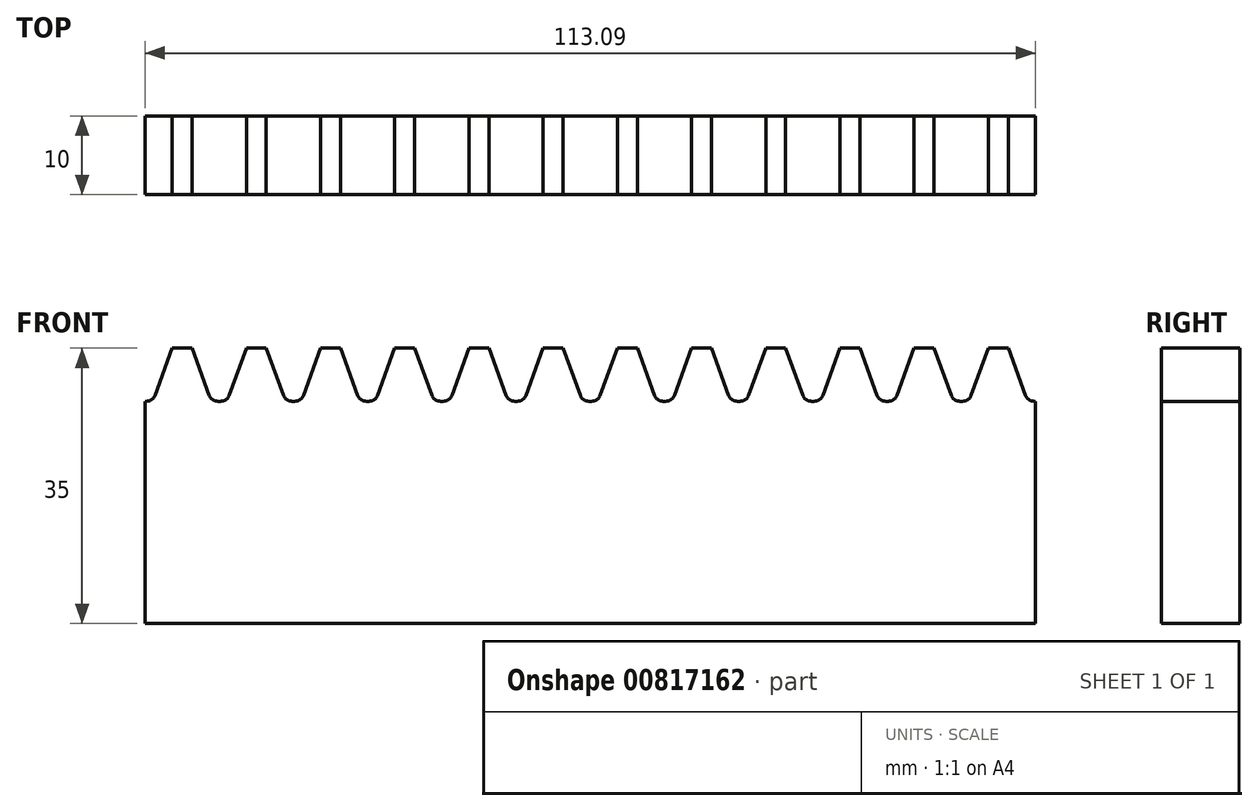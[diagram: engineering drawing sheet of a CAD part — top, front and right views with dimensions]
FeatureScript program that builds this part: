
annotation { "Feature Type Name" : "Feature", "Feature Type Description" : "" }
export const myFeature = defineFeature(function(context is Context, id is Id, definition is map)
    precondition{}
    {
        {
            assignVariable(context, id + "F0", {"name" : "Width", "anyValue" : 10 * mm});
        }
        {
            var Q0;
            Q0=qCreatedBy(makeId("Front.planeOp"),FACE);
            var sketch = newSketch(context, id + "F1", { "sketchPlane" : qUnion([Q0])});
            skLineSegment(sketch, "E0", {"start": v(1.26, 35) * mm, "end": v(-1.26, 35) * mm});
            skLineSegment(sketch, "E1", {"start": v(-4.71, 0) * mm, "end": v(4.71, 0) * mm});
            skLineSegment(sketch, "E2", {"start": v(-4.71, 28.25) * mm, "end": v(-4.52, 28.25) * mm});
            skLineSegment(sketch, "E3", {"start": v(-3.45, 29) * mm, "end": v(-1.26, 35) * mm});
            skLineSegment(sketch, "E4", {"start": v(-4.71, 28.25) * mm, "end": v(-4.71, 0) * mm});
            skLineSegment(sketch, "E5", {"start": v(-2.36, 32) * mm, "end": v(2.36, 32) * mm, "construction": true});
            skLineSegment(sketch, "E6", {"start": v(0, 35) * mm, "end": v(0, 0) * mm, "construction": true});
            skPoint(sketch, "E7.visualSharp", {"position": v(-3.72, 28.25) * mm});
            skArc(sketch, "E7.filletArc", {"start": v(-4.52, 28.25) * mm, "mid": v(-3.87, 28.46) * mm, "end": v(-3.45, 29) * mm});
            skLineSegment(sketch, "E8.MirrorCS", {"start": v(3.45, 29) * mm, "end": v(1.26, 35) * mm});
            skArc(sketch, "E9.MirrorCS", {"start": v(4.52, 28.25) * mm, "mid": v(3.87, 28.46) * mm, "end": v(3.45, 29) * mm});
            skLineSegment(sketch, "E10.MirrorCS", {"start": v(4.71, 28.25) * mm, "end": v(4.52, 28.25) * mm});
            skLineSegment(sketch, "E11.MirrorCS", {"start": v(4.71, 28.25) * mm, "end": v(4.71, 0) * mm});
            skLineSegment(sketch, "E12.1.0.0", {"start": v(9.42, 35) * mm, "end": v(9.42, 0) * mm, "construction": true});
            skPoint(sketch, "E12.1.0.2", {"position": v(5.7, 28.25) * mm});
            skLineSegment(sketch, "E12.1.0.3", {"start": v(14.14, 28.25) * mm, "end": v(14.14, 0) * mm});
            skLineSegment(sketch, "E12.1.0.4", {"start": v(12.87, 29) * mm, "end": v(10.69, 35) * mm});
            skLineSegment(sketch, "E12.1.0.5", {"start": v(4.71, 0) * mm, "end": v(14.14, 0) * mm});
            skLineSegment(sketch, "E12.1.0.6", {"start": v(7.07, 32) * mm, "end": v(11.78, 32) * mm, "construction": true});
            skLineSegment(sketch, "E12.1.0.7", {"start": v(5.98, 29) * mm, "end": v(8.16, 35) * mm});
            skLineSegment(sketch, "E12.1.0.8", {"start": v(10.69, 35) * mm, "end": v(8.16, 35) * mm});
            skArc(sketch, "E12.1.0.9", {"start": v(13.94, 28.25) * mm, "mid": v(13.3, 28.46) * mm, "end": v(12.87, 29) * mm});
            skLineSegment(sketch, "E12.1.0.10", {"start": v(14.14, 28.25) * mm, "end": v(13.94, 28.25) * mm});
            skArc(sketch, "E12.1.0.11", {"start": v(4.9, 28.25) * mm, "mid": v(5.56, 28.46) * mm, "end": v(5.98, 29) * mm});
            skLineSegment(sketch, "E12.1.0.12", {"start": v(4.71, 28.25) * mm, "end": v(4.9, 28.25) * mm});
            skLineSegment(sketch, "E12.2.0.0", {"start": v(18.85, 35) * mm, "end": v(18.85, 0) * mm, "construction": true});
            skLineSegment(sketch, "E12.2.0.1", {"start": v(14.14, 28.25) * mm, "end": v(14.14, 0) * mm});
            skPoint(sketch, "E12.2.0.2", {"position": v(15.13, 28.25) * mm});
            skLineSegment(sketch, "E12.2.0.3", {"start": v(23.56, 28.25) * mm, "end": v(23.56, 0) * mm});
            skLineSegment(sketch, "E12.2.0.4", {"start": v(22.3, 29) * mm, "end": v(20.11, 35) * mm});
            skLineSegment(sketch, "E12.2.0.5", {"start": v(14.14, 0) * mm, "end": v(23.56, 0) * mm});
            skLineSegment(sketch, "E12.2.0.6", {"start": v(16.5, 32) * mm, "end": v(21.2, 32) * mm, "construction": true});
            skLineSegment(sketch, "E12.2.0.7", {"start": v(15.4, 29) * mm, "end": v(17.59, 35) * mm});
            skLineSegment(sketch, "E12.2.0.8", {"start": v(20.11, 35) * mm, "end": v(17.59, 35) * mm});
            skArc(sketch, "E12.2.0.9", {"start": v(23.37, 28.25) * mm, "mid": v(22.71, 28.46) * mm, "end": v(22.3, 29) * mm});
            skLineSegment(sketch, "E12.2.0.10", {"start": v(23.56, 28.25) * mm, "end": v(23.37, 28.25) * mm});
            skArc(sketch, "E12.2.0.11", {"start": v(14.33, 28.25) * mm, "mid": v(14.98, 28.46) * mm, "end": v(15.4, 29) * mm});
            skLineSegment(sketch, "E12.2.0.12", {"start": v(14.14, 28.25) * mm, "end": v(14.33, 28.25) * mm});
            skLineSegment(sketch, "E12.3.0.0", {"start": v(28.27, 35) * mm, "end": v(28.27, 0) * mm, "construction": true});
            skLineSegment(sketch, "E12.3.0.1", {"start": v(23.56, 28.25) * mm, "end": v(23.56, 0) * mm});
            skPoint(sketch, "E12.3.0.2", {"position": v(24.55, 28.25) * mm});
            skLineSegment(sketch, "E12.3.0.3", {"start": v(32.99, 28.25) * mm, "end": v(32.99, 0) * mm});
            skLineSegment(sketch, "E12.3.0.4", {"start": v(31.72, 29) * mm, "end": v(29.54, 35) * mm});
            skLineSegment(sketch, "E12.3.0.5", {"start": v(23.56, 0) * mm, "end": v(32.99, 0) * mm});
            skLineSegment(sketch, "E12.3.0.6", {"start": v(25.92, 32) * mm, "end": v(30.63, 32) * mm, "construction": true});
            skLineSegment(sketch, "E12.3.0.7", {"start": v(24.83, 29) * mm, "end": v(27.01, 35) * mm});
            skLineSegment(sketch, "E12.3.0.8", {"start": v(29.54, 35) * mm, "end": v(27.01, 35) * mm});
            skArc(sketch, "E12.3.0.9", {"start": v(32.8, 28.25) * mm, "mid": v(32.14, 28.46) * mm, "end": v(31.72, 29) * mm});
            skLineSegment(sketch, "E12.3.0.10", {"start": v(32.99, 28.25) * mm, "end": v(32.8, 28.25) * mm});
            skArc(sketch, "E12.3.0.11", {"start": v(23.76, 28.25) * mm, "mid": v(24.4, 28.46) * mm, "end": v(24.83, 29) * mm});
            skLineSegment(sketch, "E12.3.0.12", {"start": v(23.56, 28.25) * mm, "end": v(23.76, 28.25) * mm});
            skLineSegment(sketch, "E12.4.0.0", {"start": v(37.7, 35) * mm, "end": v(37.7, 0) * mm, "construction": true});
            skLineSegment(sketch, "E12.4.0.1", {"start": v(32.99, 28.25) * mm, "end": v(32.99, 0) * mm});
            skPoint(sketch, "E12.4.0.2", {"position": v(33.98, 28.25) * mm});
            skLineSegment(sketch, "E12.4.0.3", {"start": v(42.41, 28.25) * mm, "end": v(42.41, 0) * mm});
            skLineSegment(sketch, "E12.4.0.4", {"start": v(41.15, 29) * mm, "end": v(38.96, 35) * mm});
            skLineSegment(sketch, "E12.4.0.5", {"start": v(32.99, 0) * mm, "end": v(42.41, 0) * mm});
            skLineSegment(sketch, "E12.4.0.6", {"start": v(35.34, 32) * mm, "end": v(40.06, 32) * mm, "construction": true});
            skLineSegment(sketch, "E12.4.0.7", {"start": v(34.25, 29) * mm, "end": v(36.43, 35) * mm});
            skLineSegment(sketch, "E12.4.0.8", {"start": v(38.96, 35) * mm, "end": v(36.43, 35) * mm});
            skArc(sketch, "E12.4.0.9", {"start": v(42.22, 28.25) * mm, "mid": v(41.56, 28.46) * mm, "end": v(41.15, 29) * mm});
            skLineSegment(sketch, "E12.4.0.10", {"start": v(42.41, 28.25) * mm, "end": v(42.22, 28.25) * mm});
            skArc(sketch, "E12.4.0.11", {"start": v(33.18, 28.25) * mm, "mid": v(33.83, 28.46) * mm, "end": v(34.25, 29) * mm});
            skLineSegment(sketch, "E12.4.0.12", {"start": v(32.99, 28.25) * mm, "end": v(33.18, 28.25) * mm});
            skLineSegment(sketch, "E12.5.0.0", {"start": v(47.12, 35) * mm, "end": v(47.12, 0) * mm, "construction": true});
            skLineSegment(sketch, "E12.5.0.1", {"start": v(42.41, 28.25) * mm, "end": v(42.41, 0) * mm});
            skPoint(sketch, "E12.5.0.2", {"position": v(43.4, 28.25) * mm});
            skLineSegment(sketch, "E12.5.0.3", {"start": v(51.84, 28.25) * mm, "end": v(51.84, 0) * mm});
            skLineSegment(sketch, "E12.5.0.4", {"start": v(50.57, 29) * mm, "end": v(48.39, 35) * mm});
            skLineSegment(sketch, "E12.5.0.5", {"start": v(42.41, 0) * mm, "end": v(51.84, 0) * mm});
            skLineSegment(sketch, "E12.5.0.6", {"start": v(44.77, 32) * mm, "end": v(49.48, 32) * mm, "construction": true});
            skLineSegment(sketch, "E12.5.0.7", {"start": v(43.68, 29) * mm, "end": v(45.86, 35) * mm});
            skLineSegment(sketch, "E12.5.0.8", {"start": v(48.39, 35) * mm, "end": v(45.86, 35) * mm});
            skArc(sketch, "E12.5.0.9", {"start": v(51.64, 28.25) * mm, "mid": v(50.99, 28.46) * mm, "end": v(50.57, 29) * mm});
            skLineSegment(sketch, "E12.5.0.10", {"start": v(51.84, 28.25) * mm, "end": v(51.64, 28.25) * mm});
            skArc(sketch, "E12.5.0.11", {"start": v(42.6, 28.25) * mm, "mid": v(43.26, 28.46) * mm, "end": v(43.68, 29) * mm});
            skLineSegment(sketch, "E12.5.0.12", {"start": v(42.41, 28.25) * mm, "end": v(42.6, 28.25) * mm});
            skLineSegment(sketch, "E12.6.0.0", {"start": v(56.55, 35) * mm, "end": v(56.55, 0) * mm, "construction": true});
            skLineSegment(sketch, "E12.6.0.1", {"start": v(51.84, 28.25) * mm, "end": v(51.84, 0) * mm});
            skPoint(sketch, "E12.6.0.2", {"position": v(52.83, 28.25) * mm});
            skLineSegment(sketch, "E12.6.0.3", {"start": v(61.26, 28.25) * mm, "end": v(61.26, 0) * mm});
            skLineSegment(sketch, "E12.6.0.4", {"start": v(60, 29) * mm, "end": v(57.81, 35) * mm});
            skLineSegment(sketch, "E12.6.0.5", {"start": v(51.84, 0) * mm, "end": v(61.26, 0) * mm});
            skLineSegment(sketch, "E12.6.0.6", {"start": v(54.2, 32) * mm, "end": v(58.9, 32) * mm, "construction": true});
            skLineSegment(sketch, "E12.6.0.7", {"start": v(53.1, 29) * mm, "end": v(55.28, 35) * mm});
            skLineSegment(sketch, "E12.6.0.8", {"start": v(57.81, 35) * mm, "end": v(55.28, 35) * mm});
            skArc(sketch, "E12.6.0.9", {"start": v(61.07, 28.25) * mm, "mid": v(60.41, 28.46) * mm, "end": v(60, 29) * mm});
            skLineSegment(sketch, "E12.6.0.10", {"start": v(61.26, 28.25) * mm, "end": v(61.07, 28.25) * mm});
            skArc(sketch, "E12.6.0.11", {"start": v(52.03, 28.25) * mm, "mid": v(52.68, 28.46) * mm, "end": v(53.1, 29) * mm});
            skLineSegment(sketch, "E12.6.0.12", {"start": v(51.84, 28.25) * mm, "end": v(52.03, 28.25) * mm});
            skLineSegment(sketch, "E12.7.0.0", {"start": v(65.97, 35) * mm, "end": v(65.97, 0) * mm, "construction": true});
            skLineSegment(sketch, "E12.7.0.1", {"start": v(61.26, 28.25) * mm, "end": v(61.26, 0) * mm});
            skPoint(sketch, "E12.7.0.2", {"position": v(62.25, 28.25) * mm});
            skLineSegment(sketch, "E12.7.0.3", {"start": v(70.69, 28.25) * mm, "end": v(70.69, 0) * mm});
            skLineSegment(sketch, "E12.7.0.4", {"start": v(69.42, 29) * mm, "end": v(67.24, 35) * mm});
            skLineSegment(sketch, "E12.7.0.5", {"start": v(61.26, 0) * mm, "end": v(70.69, 0) * mm});
            skLineSegment(sketch, "E12.7.0.6", {"start": v(63.62, 32) * mm, "end": v(68.33, 32) * mm, "construction": true});
            skLineSegment(sketch, "E12.7.0.7", {"start": v(62.53, 29) * mm, "end": v(64.7, 35) * mm});
            skLineSegment(sketch, "E12.7.0.8", {"start": v(67.24, 35) * mm, "end": v(64.7, 35) * mm});
            skArc(sketch, "E12.7.0.9", {"start": v(70.5, 28.25) * mm, "mid": v(69.84, 28.46) * mm, "end": v(69.42, 29) * mm});
            skLineSegment(sketch, "E12.7.0.10", {"start": v(70.69, 28.25) * mm, "end": v(70.5, 28.25) * mm});
            skArc(sketch, "E12.7.0.11", {"start": v(61.45, 28.25) * mm, "mid": v(62.1, 28.46) * mm, "end": v(62.53, 29) * mm});
            skLineSegment(sketch, "E12.7.0.12", {"start": v(61.26, 28.25) * mm, "end": v(61.45, 28.25) * mm});
            skLineSegment(sketch, "E12.8.0.0", {"start": v(75.4, 35) * mm, "end": v(75.4, 0) * mm, "construction": true});
            skLineSegment(sketch, "E12.8.0.1", {"start": v(70.69, 28.25) * mm, "end": v(70.69, 0) * mm});
            skPoint(sketch, "E12.8.0.2", {"position": v(71.68, 28.25) * mm});
            skLineSegment(sketch, "E12.8.0.3", {"start": v(80.11, 28.25) * mm, "end": v(80.11, 0) * mm});
            skLineSegment(sketch, "E12.8.0.4", {"start": v(78.85, 29) * mm, "end": v(76.66, 35) * mm});
            skLineSegment(sketch, "E12.8.0.5", {"start": v(70.69, 0) * mm, "end": v(80.11, 0) * mm});
            skLineSegment(sketch, "E12.8.0.6", {"start": v(73.04, 32) * mm, "end": v(77.75, 32) * mm, "construction": true});
            skLineSegment(sketch, "E12.8.0.7", {"start": v(71.95, 29) * mm, "end": v(74.13, 35) * mm});
            skLineSegment(sketch, "E12.8.0.8", {"start": v(76.66, 35) * mm, "end": v(74.13, 35) * mm});
            skArc(sketch, "E12.8.0.9", {"start": v(79.92, 28.25) * mm, "mid": v(79.26, 28.46) * mm, "end": v(78.85, 29) * mm});
            skLineSegment(sketch, "E12.8.0.10", {"start": v(80.11, 28.25) * mm, "end": v(79.92, 28.25) * mm});
            skArc(sketch, "E12.8.0.11", {"start": v(70.88, 28.25) * mm, "mid": v(71.53, 28.46) * mm, "end": v(71.95, 29) * mm});
            skLineSegment(sketch, "E12.8.0.12", {"start": v(70.69, 28.25) * mm, "end": v(70.88, 28.25) * mm});
            skLineSegment(sketch, "E12.9.0.0", {"start": v(84.82, 35) * mm, "end": v(84.82, 0) * mm, "construction": true});
            skLineSegment(sketch, "E12.9.0.1", {"start": v(80.11, 28.25) * mm, "end": v(80.11, 0) * mm});
            skPoint(sketch, "E12.9.0.2", {"position": v(81.1, 28.25) * mm});
            skLineSegment(sketch, "E12.9.0.3", {"start": v(89.54, 28.25) * mm, "end": v(89.54, 0) * mm});
            skLineSegment(sketch, "E12.9.0.4", {"start": v(88.27, 29) * mm, "end": v(86.09, 35) * mm});
            skLineSegment(sketch, "E12.9.0.5", {"start": v(80.11, 0) * mm, "end": v(89.54, 0) * mm});
            skLineSegment(sketch, "E12.9.0.6", {"start": v(82.47, 32) * mm, "end": v(87.18, 32) * mm, "construction": true});
            skLineSegment(sketch, "E12.9.0.7", {"start": v(81.37, 29) * mm, "end": v(83.56, 35) * mm});
            skLineSegment(sketch, "E12.9.0.8", {"start": v(86.09, 35) * mm, "end": v(83.56, 35) * mm});
            skArc(sketch, "E12.9.0.9", {"start": v(89.34, 28.25) * mm, "mid": v(88.69, 28.46) * mm, "end": v(88.27, 29) * mm});
            skLineSegment(sketch, "E12.9.0.10", {"start": v(89.54, 28.25) * mm, "end": v(89.34, 28.25) * mm});
            skArc(sketch, "E12.9.0.11", {"start": v(80.3, 28.25) * mm, "mid": v(80.96, 28.46) * mm, "end": v(81.37, 29) * mm});
            skLineSegment(sketch, "E12.9.0.12", {"start": v(80.11, 28.25) * mm, "end": v(80.3, 28.25) * mm});
            skLineSegment(sketch, "E12.10.0.0", {"start": v(94.25, 35) * mm, "end": v(94.25, 0) * mm, "construction": true});
            skLineSegment(sketch, "E12.10.0.1", {"start": v(89.54, 28.25) * mm, "end": v(89.54, 0) * mm});
            skPoint(sketch, "E12.10.0.2", {"position": v(90.53, 28.25) * mm});
            skLineSegment(sketch, "E12.10.0.3", {"start": v(98.96, 28.25) * mm, "end": v(98.96, 0) * mm});
            skLineSegment(sketch, "E12.10.0.4", {"start": v(97.7, 29) * mm, "end": v(95.51, 35) * mm});
            skLineSegment(sketch, "E12.10.0.5", {"start": v(89.54, 0) * mm, "end": v(98.96, 0) * mm});
            skLineSegment(sketch, "E12.10.0.6", {"start": v(91.9, 32) * mm, "end": v(96.6, 32) * mm, "construction": true});
            skLineSegment(sketch, "E12.10.0.7", {"start": v(90.8, 29) * mm, "end": v(92.98, 35) * mm});
            skLineSegment(sketch, "E12.10.0.8", {"start": v(95.51, 35) * mm, "end": v(92.98, 35) * mm});
            skArc(sketch, "E12.10.0.9", {"start": v(98.77, 28.25) * mm, "mid": v(98.11, 28.46) * mm, "end": v(97.7, 29) * mm});
            skLineSegment(sketch, "E12.10.0.10", {"start": v(98.96, 28.25) * mm, "end": v(98.77, 28.25) * mm});
            skArc(sketch, "E12.10.0.11", {"start": v(89.73, 28.25) * mm, "mid": v(90.38, 28.46) * mm, "end": v(90.8, 29) * mm});
            skLineSegment(sketch, "E12.10.0.12", {"start": v(89.54, 28.25) * mm, "end": v(89.73, 28.25) * mm});
            skLineSegment(sketch, "E12.11.0.0", {"start": v(103.67, 35) * mm, "end": v(103.67, 0) * mm, "construction": true});
            skLineSegment(sketch, "E12.11.0.1", {"start": v(98.96, 28.25) * mm, "end": v(98.96, 0) * mm});
            skPoint(sketch, "E12.11.0.2", {"position": v(99.95, 28.25) * mm});
            skLineSegment(sketch, "E12.11.0.3", {"start": v(108.38, 28.25) * mm, "end": v(108.38, 0) * mm});
            skLineSegment(sketch, "E12.11.0.4", {"start": v(107.12, 29) * mm, "end": v(104.94, 35) * mm});
            skLineSegment(sketch, "E12.11.0.5", {"start": v(98.96, 0) * mm, "end": v(108.38, 0) * mm});
            skLineSegment(sketch, "E12.11.0.6", {"start": v(101.32, 32) * mm, "end": v(106.03, 32) * mm, "construction": true});
            skLineSegment(sketch, "E12.11.0.7", {"start": v(100.22, 29) * mm, "end": v(102.4, 35) * mm});
            skLineSegment(sketch, "E12.11.0.8", {"start": v(104.94, 35) * mm, "end": v(102.4, 35) * mm});
            skArc(sketch, "E12.11.0.9", {"start": v(108.2, 28.25) * mm, "mid": v(107.54, 28.46) * mm, "end": v(107.12, 29) * mm});
            skLineSegment(sketch, "E12.11.0.10", {"start": v(108.38, 28.25) * mm, "end": v(108.2, 28.25) * mm});
            skArc(sketch, "E12.11.0.11", {"start": v(99.15, 28.25) * mm, "mid": v(99.8, 28.46) * mm, "end": v(100.22, 29) * mm});
            skLineSegment(sketch, "E12.11.0.12", {"start": v(98.96, 28.25) * mm, "end": v(99.15, 28.25) * mm});
            skLineSegment(sketch, "E12.direction1", {"start": v(-4.71, 0) * mm, "end": v(4.71, 0) * mm, "construction": true});
            skSolve(sketch);
        }
        {
            var Q0;
            Q0 = qSketchRegion(id + "F1", true);
            extrude(context, id + "F2", {"entities" : qUnion([Q0]), "depth" : getVariable(context, 'Width'), "offsetDistance" : 25 * mm});
        }
    });
